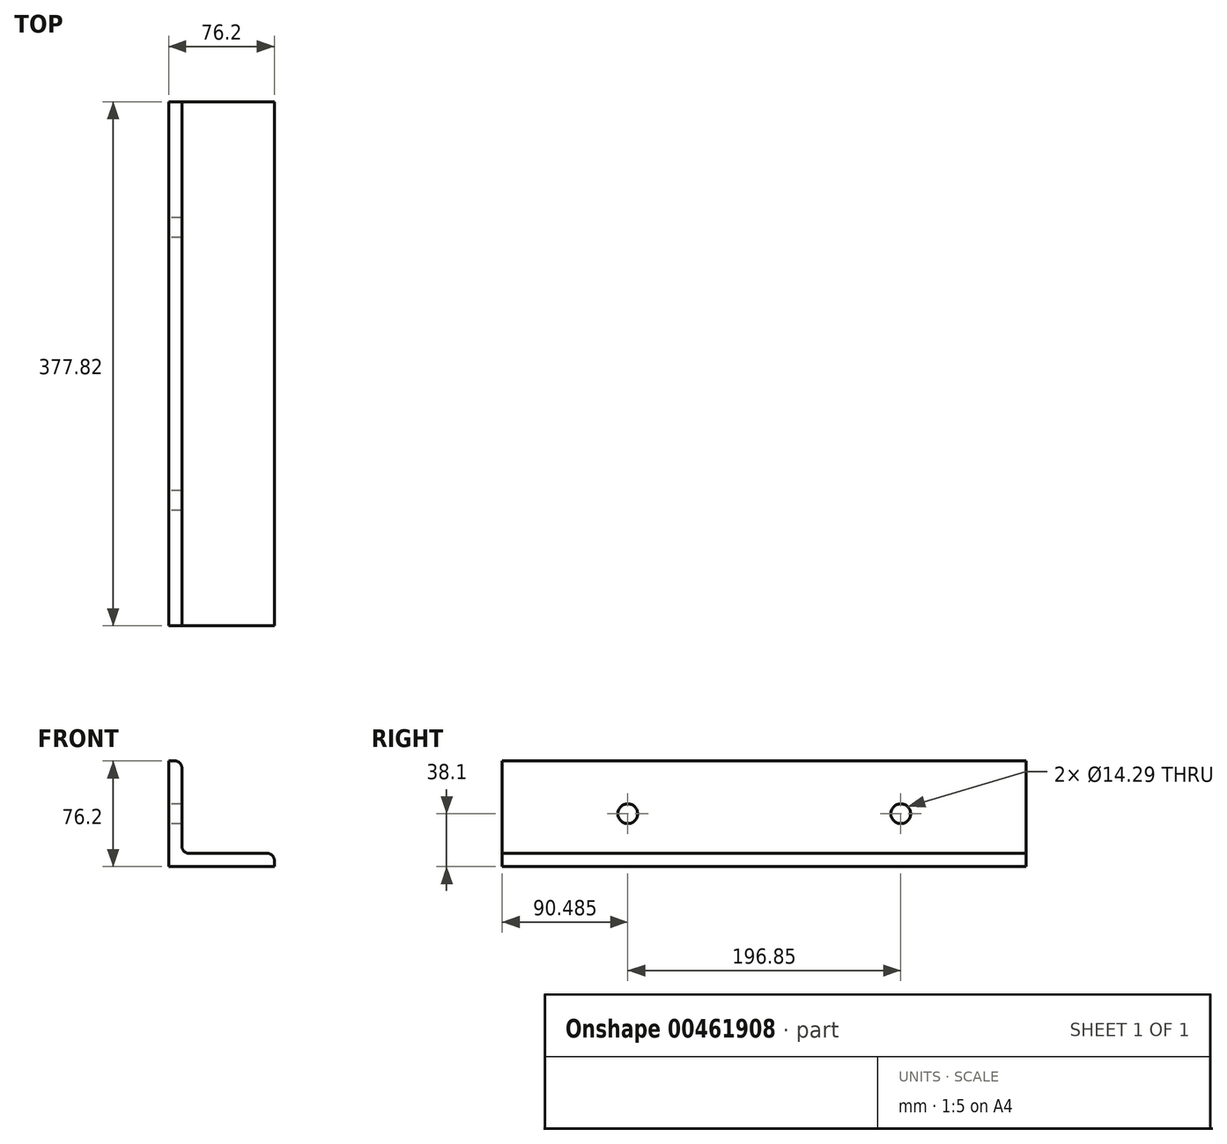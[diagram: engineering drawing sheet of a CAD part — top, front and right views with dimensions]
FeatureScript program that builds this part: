
annotation { "Feature Type Name" : "Feature", "Feature Type Description" : "" }
export const myFeature = defineFeature(function(context is Context, id is Id, definition is map)
    precondition{}
    {
        {
            var Q0;
            Q0=qCreatedBy(makeId("Front.planeOp"),FACE);
            var sketch = newSketch(context, id + "F0", { "sketchPlane" : qUnion([Q0])});
            skLineSegment(sketch, "E0.bottom", {"start": v(38.1, -38.1) * mm, "end": v(-38.1, -38.1) * mm});
            skLineSegment(sketch, "E0.top", {"start": v(-28.57, 38.1) * mm, "end": v(-38.1, 38.1) * mm});
            skLineSegment(sketch, "E0.left", {"start": v(38.1, -38.1) * mm, "end": v(38.1, -28.57) * mm});
            skLineSegment(sketch, "E0.right", {"start": v(-38.1, -38.1) * mm, "end": v(-38.1, 38.1) * mm});
            skPoint(sketch, "E0.middle", {"position": v(0, 0) * mm});
            skLineSegment(sketch, "E1.0", {"start": v(-28.58, -28.58) * mm, "end": v(-28.57, 38.1) * mm});
            skLineSegment(sketch, "E2.0", {"start": v(38.1, -28.57) * mm, "end": v(-28.57, -28.58) * mm});
            skPoint(sketch, "E3.orphan", {"position": v(38.1, 38.1) * mm});
            skSolve(sketch);
        }
        {
            var Q0;
            Q0 = qSketchRegion(id + "F0", true);
            extrude(context, id + "F1", {"entities" : qUnion([Q0]), "endBound" : BoundingType.SYMMETRIC, "depth" : 377.82 * mm});
        }
        {
            var Q0;
            Q0=makeQuery(id+"F1.opExtrude","SWEPT_EDGE",EDGE,{"disambiguationData":[OSD([sQuery(id+"F0.wireOp",EDGE,"E0.top"),sQuery(id+"F0.wireOp",EDGE,"E1.0")])]});
            var Q1;
            Q1=makeQuery(id+"F1.opExtrude","SWEPT_EDGE",EDGE,{"disambiguationData":[OSD([sQuery(id+"F0.wireOp",EDGE,"E1.0"),sQuery(id+"F0.wireOp",EDGE,"E2.0")])]});
            var Q2;
            Q2=makeQuery(id+"F1.opExtrude","SWEPT_EDGE",EDGE,{"disambiguationData":[OSD([sQuery(id+"F0.wireOp",EDGE,"E0.left"),sQuery(id+"F0.wireOp",EDGE,"E2.0")])]});
            fillet(context, id + "F2", {"entities" : qUnion([Q0, Q1, Q2]), "radius" : 5.08 * mm, "tangentPropagation" : true, "allowEdgeOverflow" : false});
        }
        {
            var Q0;
            Q0=makeQuery(id+"F1.opExtrude","SWEPT_FACE",FACE,{"disambiguationData":[OSD([sQuery(id+"F0.wireOp",EDGE,"E0.right")])]});
            var sketch = newSketch(context, id + "F3", { "sketchPlane" : qUnion([Q0])});
            skCircle(sketch, "E4", {"center": v(-98.43, 0) * mm, "radius": 7.14 * mm});
            skCircle(sketch, "E5", {"center": v(98.43, 0) * mm, "radius": 7.14 * mm});
            skSolve(sketch);
        }
        {
            var Q0;
            Q0=makeQuery(id+"F3.imprint","IMPRINT",FACE,{"disambiguationData":[TD([[makeQuery(id+"F3.imprint","IMPRINT",EDGE,{"derivedFrom":sQuery(id+"F3.wireOp",EDGE,"E4")}),1.0]])]});
            var Q1;
            Q1=makeQuery(id+"F3.imprint","IMPRINT",FACE,{"disambiguationData":[TD([[makeQuery(id+"F3.imprint","IMPRINT",EDGE,{"derivedFrom":sQuery(id+"F3.wireOp",EDGE,"E5")}),1.0]])]});
            var Q2;
            Q2=sQuery(id+"F3.wireOp",EDGE,"E4");
            var Q3;
            Q3=sQuery(id+"F3.wireOp",EDGE,"E5");
            extrude(context, id + "F4", {"entities" : qUnion([Q0, Q1]), "operationType" : NewBodyOperationType.REMOVE, "surfaceEntities" : qUnion([Q2, Q3]), "oppositeDirection" : true, "depth" : 25.4 * mm});
        }
    });
